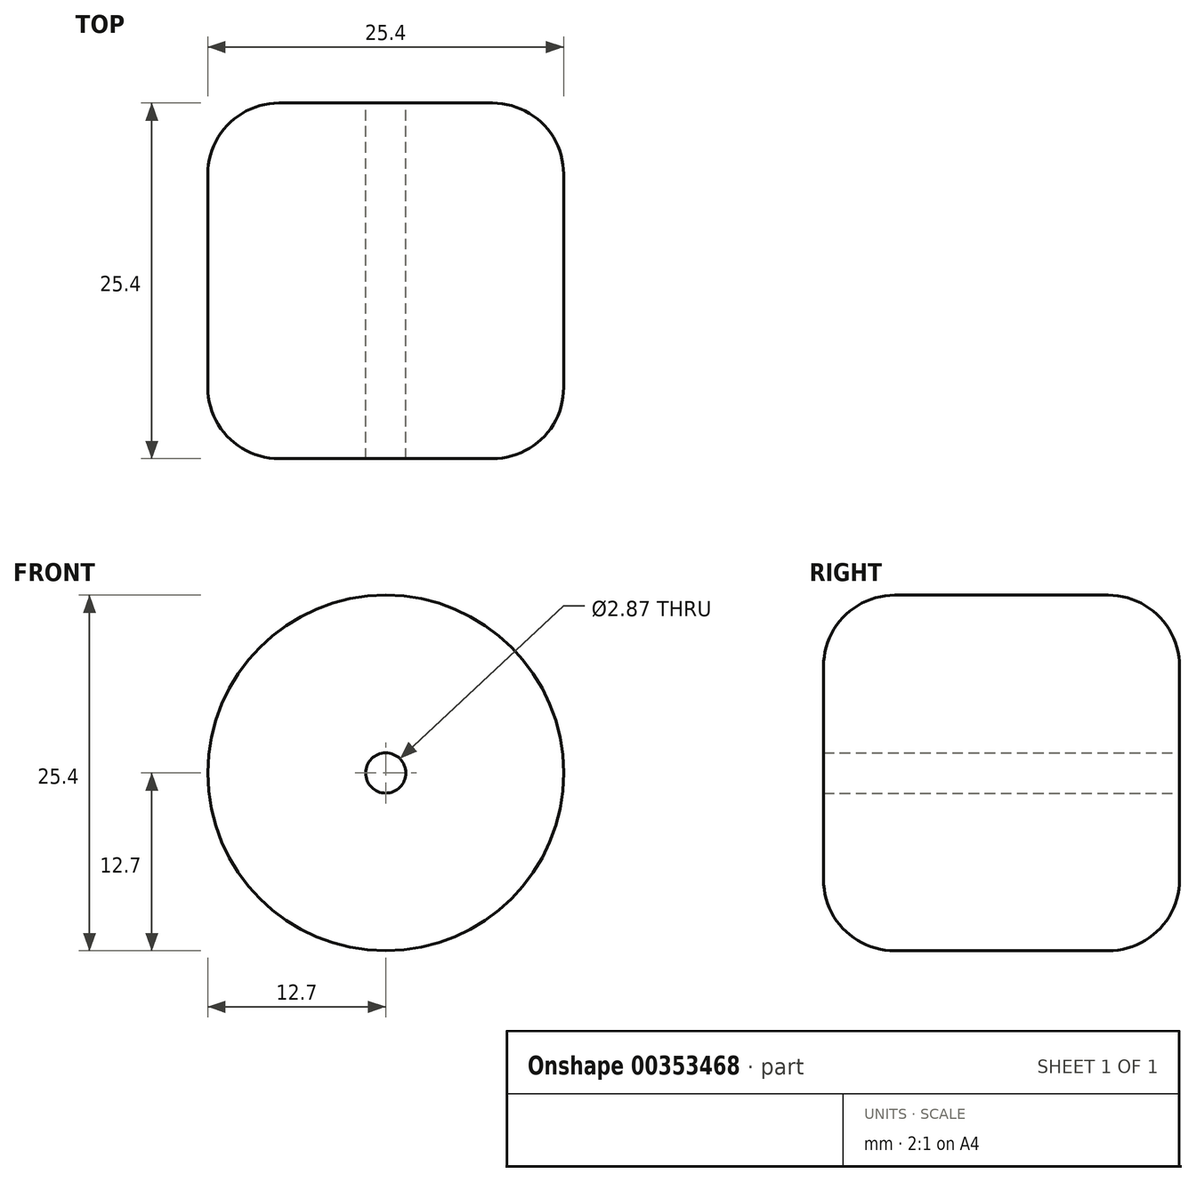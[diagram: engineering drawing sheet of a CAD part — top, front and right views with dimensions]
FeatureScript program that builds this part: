
annotation { "Feature Type Name" : "Feature", "Feature Type Description" : "" }
export const myFeature = defineFeature(function(context is Context, id is Id, definition is map)
    precondition{}
    {
        {
            var Q0;
            Q0=qCreatedBy(makeId("Front.planeOp"),FACE);
            var sketch = newSketch(context, id + "F0", { "sketchPlane" : qUnion([Q0])});
            skCircle(sketch, "E0", {"center": v(0, 0) * mm, "radius": 12.7 * mm});
            skSolve(sketch);
        }
        {
            var Q0;
            Q0 = qSketchRegion(id + "F0", true);
            extrude(context, id + "F1", {"entities" : qUnion([Q0]), "depth" : 25.4 * mm});
        }
        {
            var Q0;
            Q0 = qSketchRegion(id + "F0", true);
            extrude(context, id + "F2", {"entities" : qUnion([Q0]), "operationType" : NewBodyOperationType.ADD, "depth" : 17.78 * mm});
        }
        {
            var Q0;
            Q0=makeQuery(id+"F1.opExtrude","CAP_EDGE",EDGE,{"disambiguationData":[OSD([sQuery(id+"F0.wireOp",EDGE,"E0")])],"isStart":true});
            var Q1;
            Q1=makeQuery(id+"F1.opExtrude","CAP_EDGE",EDGE,{"disambiguationData":[OSD([sQuery(id+"F0.wireOp",EDGE,"E0")])],"isStart":false});
            fillet(context, id + "F3", {"entities" : qUnion([Q0, Q1]), "radius" : 5.08 * mm, "tangentPropagation" : true, "allowEdgeOverflow" : false});
        }
        {
            var Q0;
            Q0=makeQuery(id+"F1.opExtrude","CAP_FACE",FACE,{"disambiguationData":[OSD([sQuery(id+"F0.wireOp",EDGE,"E0")])],"isStart":true});
            var sketch = newSketch(context, id + "F4", { "sketchPlane" : qUnion([Q0])});
            skCircle(sketch, "E1", {"center": v(0, 0) * mm, "radius": 1.44 * mm});
            skSolve(sketch);
        }
        {
            var Q0;
            Q0=makeQuery(id+"F4.imprint","IMPRINT",FACE,{"disambiguationData":[TD([[makeQuery(id+"F4.imprint","IMPRINT",EDGE,{"derivedFrom":sQuery(id+"F4.wireOp",EDGE,"E1")}),1.0]])]});
            extrude(context, id + "F5", {"entities" : qUnion([Q0]), "operationType" : NewBodyOperationType.REMOVE, "oppositeDirection" : true, "depth" : 25.4 * mm});
        }
    });
